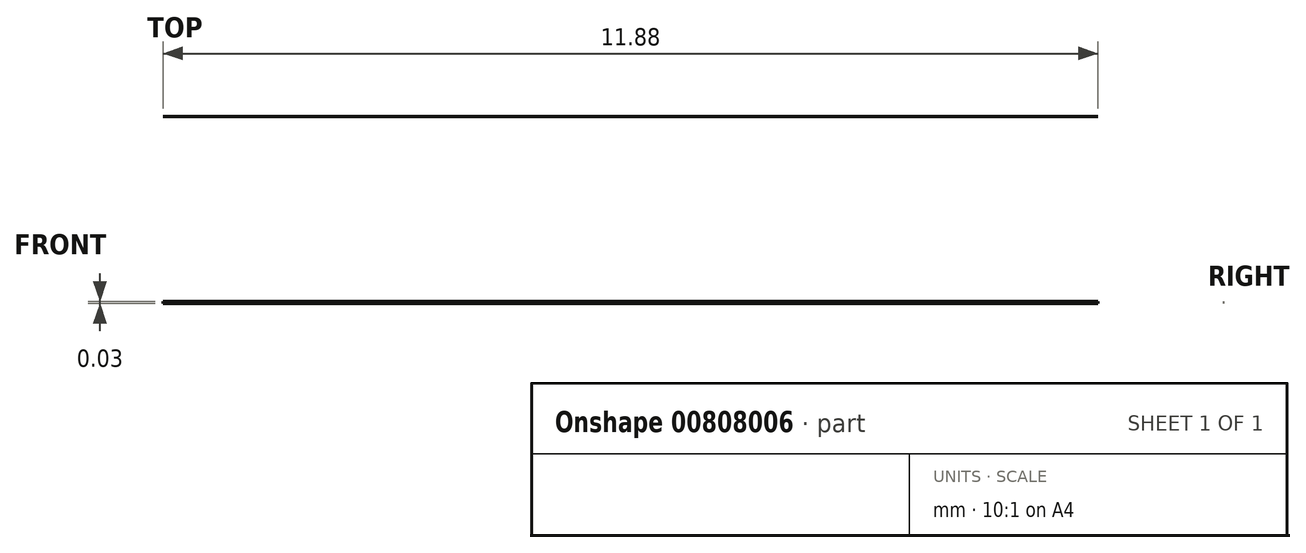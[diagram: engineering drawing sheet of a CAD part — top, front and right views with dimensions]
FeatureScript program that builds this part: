
annotation { "Feature Type Name" : "Feature", "Feature Type Description" : "" }
export const myFeature = defineFeature(function(context is Context, id is Id, definition is map)
    precondition{}
    {
        {
            var Q0;
            Q0=qCreatedBy(makeId("Right.planeOp"),FACE);
            var sketch = newSketch(context, id + "F0", { "sketchPlane" : qUnion([Q0])});
            skLineSegment(sketch, "E0.0.0", {"start": v(-9.52, -7.25) * mm, "end": v(9.53, -7.25) * mm});
            skLineSegment(sketch, "E0.0.1", {"start": v(9.53, -7.25) * mm, "end": v(9.53, 1.76) * mm});
            skLineSegment(sketch, "E0.0.2", {"start": v(9.02, 2.27) * mm, "end": v(5.14, 2.27) * mm});
            skLineSegment(sketch, "E0.0.3", {"start": v(4.63, 1.76) * mm, "end": v(4.63, 0.62) * mm});
            skLineSegment(sketch, "E0.0.4", {"start": v(4.63, 0.62) * mm, "end": v(6.22, 0.62) * mm});
            skLineSegment(sketch, "E0.0.5", {"start": v(6.22, 0.62) * mm, "end": v(6.22, -2.82) * mm});
            skLineSegment(sketch, "E0.0.6", {"start": v(6.22, -2.82) * mm, "end": v(4.63, -2.82) * mm});
            skLineSegment(sketch, "E0.0.7", {"start": v(4.63, -2.82) * mm, "end": v(4.63, -5.27) * mm});
            skLineSegment(sketch, "E0.0.8", {"start": v(4.63, -5.27) * mm, "end": v(-4.63, -5.27) * mm});
            skLineSegment(sketch, "E0.0.9", {"start": v(-4.63, -5.27) * mm, "end": v(-4.63, -2.82) * mm});
            skLineSegment(sketch, "E0.0.10", {"start": v(-4.63, -2.82) * mm, "end": v(-6.22, -2.82) * mm});
            skLineSegment(sketch, "E0.0.11", {"start": v(-6.22, -2.82) * mm, "end": v(-6.22, 0.62) * mm});
            skLineSegment(sketch, "E0.0.12", {"start": v(-6.22, 0.62) * mm, "end": v(-4.63, 0.62) * mm});
            skLineSegment(sketch, "E0.0.13", {"start": v(-4.63, 0.62) * mm, "end": v(-4.63, 1.76) * mm});
            skLineSegment(sketch, "E0.0.14", {"start": v(-5.14, 2.27) * mm, "end": v(-9.17, 2.27) * mm});
            skLineSegment(sketch, "E0.0.15", {"start": v(-9.52, 1.92) * mm, "end": v(-9.52, -7.25) * mm});
            skLineSegment(sketch, "E1", {"start": v(-9.52, -7.25) * mm, "end": v(-28.57, -7.25) * mm});
            skLineSegment(sketch, "E2", {"start": v(-28.57, -7.25) * mm, "end": v(-28.57, 1.76) * mm});
            skLineSegment(sketch, "E3", {"start": v(-28.07, 2.27) * mm, "end": v(-26.96, 2.27) * mm});
            skLineSegment(sketch, "E4", {"start": v(-26.46, 1.76) * mm, "end": v(-26.46, 0.67) * mm});
            skLineSegment(sketch, "E5", {"start": v(-26.46, 0.67) * mm, "end": v(-19.4, 0.67) * mm});
            skLineSegment(sketch, "E6", {"start": v(-11.64, 0.67) * mm, "end": v(-11.64, 1.76) * mm});
            skLineSegment(sketch, "E7", {"start": v(-11.14, 2.27) * mm, "end": v(-9.88, 2.27) * mm});
            skArc(sketch, "E8", {"start": v(-19.4, 0.67) * mm, "mid": v(-19.05, 0.32) * mm, "end": v(-18.7, 0.67) * mm});
            skLineSegment(sketch, "E9.trimOffspring", {"start": v(-18.7, 0.67) * mm, "end": v(-11.64, 0.67) * mm});
            skArc(sketch, "E10", {"start": v(-9.88, 2.27) * mm, "mid": v(-9.52, 1.92) * mm, "end": v(-9.17, 2.27) * mm});
            skPoint(sketch, "E11.visualSharp", {"position": v(9.53, 2.27) * mm});
            skArc(sketch, "E11.filletArc", {"start": v(9.53, 1.76) * mm, "mid": v(9.38, 2.12) * mm, "end": v(9.02, 2.27) * mm});
            skPoint(sketch, "E12.visualSharp", {"position": v(-28.57, 2.27) * mm});
            skArc(sketch, "E12.filletArc", {"start": v(-28.07, 2.27) * mm, "mid": v(-28.43, 2.12) * mm, "end": v(-28.57, 1.76) * mm});
            skPoint(sketch, "E13.visualSharp", {"position": v(-11.64, 2.27) * mm});
            skArc(sketch, "E13.filletArc", {"start": v(-11.14, 2.27) * mm, "mid": v(-11.5, 2.12) * mm, "end": v(-11.64, 1.76) * mm});
            skPoint(sketch, "E14.visualSharp", {"position": v(-4.63, 2.27) * mm});
            skArc(sketch, "E14.filletArc", {"start": v(-4.63, 1.76) * mm, "mid": v(-4.78, 2.12) * mm, "end": v(-5.14, 2.27) * mm});
            skPoint(sketch, "E15.visualSharp", {"position": v(-26.46, 2.27) * mm});
            skArc(sketch, "E15.filletArc", {"start": v(-26.46, 1.76) * mm, "mid": v(-26.6, 2.12) * mm, "end": v(-26.96, 2.27) * mm});
            skPoint(sketch, "E16.visualSharp", {"position": v(4.63, 2.27) * mm});
            skArc(sketch, "E16.filletArc", {"start": v(5.14, 2.27) * mm, "mid": v(4.78, 2.12) * mm, "end": v(4.63, 1.76) * mm});
            skSolve(sketch);
        }
        {
            var Q0;
            Q0=qSketchRegion(id+"F0",true);
            extrude(context, id + "F1", {"entities" : qUnion([Q0]), "oppositeDirection" : true, "depth" : (11 + (7 / 8)) * mm, "offsetDistance" : 25.4 * mm});
        }
        {
            var Q0;
            Q0=makeQuery(id+"F1.opExtrude","SWEPT_FACE",FACE,{"disambiguationData":[OSD([sQuery(id+"F0.wireOp",EDGE,"E0.0.0"),sQuery(id+"F0.wireOp",EDGE,"E1")])]});
            var sketch = newSketch(context, id + "F2", { "sketchPlane" : qUnion([Q0])});
            skLineSegment(sketch, "E17", {"start": v(-301.63, 28.58) * mm, "end": v(-246.08, -26.97) * mm});
            skSolve(sketch);
        }
        {
            var Q0;
            Q0 = qSketchRegion(id + "F2", true);
            var Q1;
            {var subQ1=sQuery(id+"F0.wireOp",EDGE,"E1");var subQ2=sQuery(id+"F0.wireOp",EDGE,"E0.0.0");var subQ3=makeQuery(id+"F1.opExtrude","CAP_EDGE",EDGE,{"disambiguationData":[OSD([subQ2,subQ1])],"isStart":false});Q1=makeQuery(id+"F2.imprint","IMPRINT",FACE,{"disambiguationData":[TD([[makeQuery(id+"F2.imprint","IMPRINT",EDGE,{"derivedFrom":subQ3}),1.0]])]});}
            extrude(context, id + "F3", {"entities" : qUnion([Q0, Q1]), "operationType" : NewBodyOperationType.REMOVE, "oppositeDirection" : true, "depth" : 25.4 * mm, "offsetDistance" : 25.4 * mm});
        }
    });
